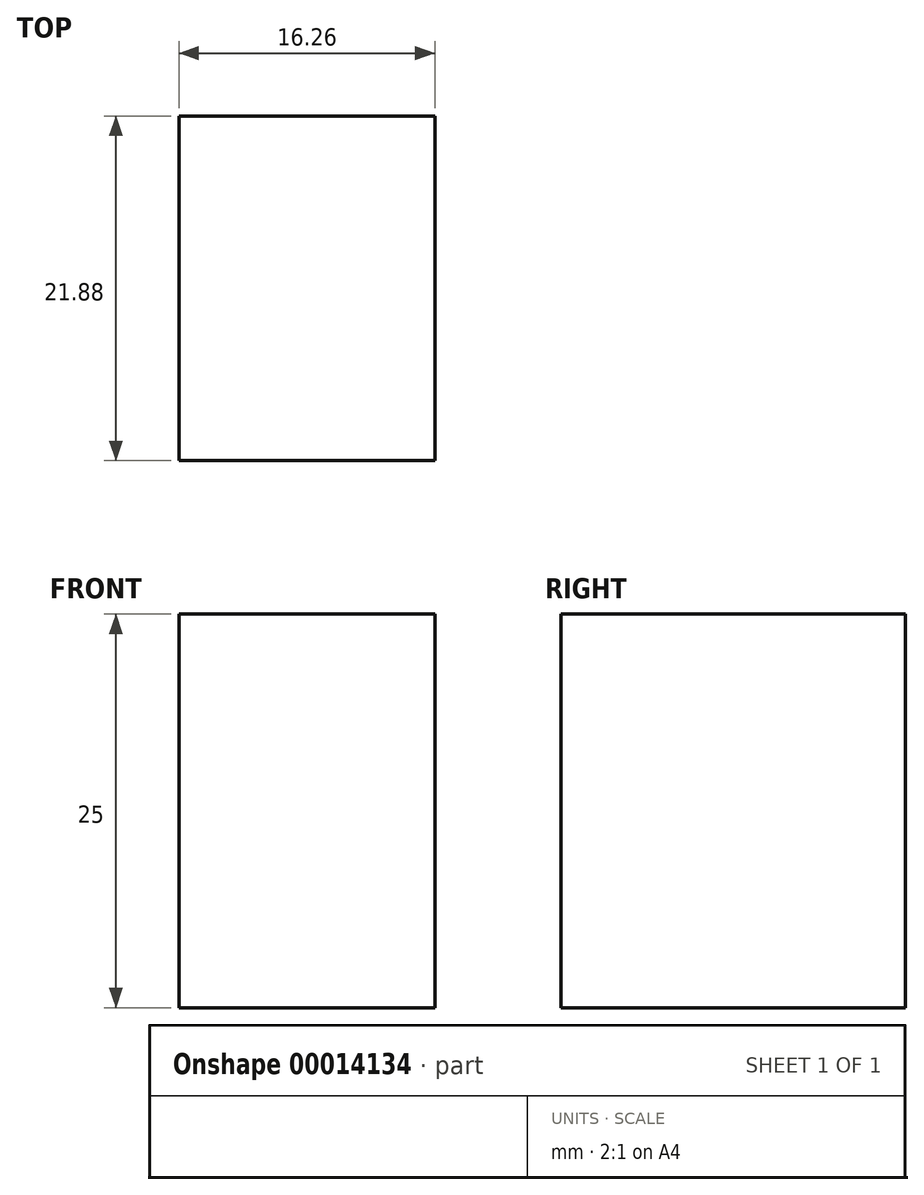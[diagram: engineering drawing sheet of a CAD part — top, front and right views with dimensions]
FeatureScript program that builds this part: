
annotation { "Feature Type Name" : "Feature", "Feature Type Description" : "" }
export const myFeature = defineFeature(function(context is Context, id is Id, definition is map)
    precondition{}
    {
        {
            var Q0;
            Q0=qCreatedBy(makeId("Front.planeOp"),FACE);
            var sketch = newSketch(context, id + "F0", { "sketchPlane" : qUnion([Q0])});
            skLineSegment(sketch, "E0", {"start": v(0, 0) * mm, "end": v(0, 450) * mm});
            skLineSegment(sketch, "E1", {"start": v(0, 0) * mm, "end": v(450, 0) * mm});
            skSolve(sketch);
        }
        {
            var Q0;
            Q0=qCreatedBy(makeId("Top.planeOp"),FACE);
            var sketch = newSketch(context, id + "F1", { "sketchPlane" : qUnion([Q0])});
            skLineSegment(sketch, "E2.rect.bottom", {"start": v(8.13, 10.94) * mm, "end": v(-8.13, 10.94) * mm});
            skLineSegment(sketch, "E2.rect.top", {"start": v(8.13, -10.94) * mm, "end": v(-8.13, -10.94) * mm});
            skLineSegment(sketch, "E2.rect.left", {"start": v(8.13, 10.94) * mm, "end": v(8.13, -10.94) * mm});
            skLineSegment(sketch, "E2.rect.right", {"start": v(-8.13, 10.94) * mm, "end": v(-8.13, -10.94) * mm});
            skPoint(sketch, "E2.rect.middle", {"position": v(0, 0) * mm});
            skSolve(sketch);
        }
        {
            var Q0;
            Q0=qSketchRegion(id+"F1",true);
            extrude(context, id + "F2", {"entities" : qUnion([Q0]), "endBound" : BoundingType.SYMMETRIC, "depth" : 25 * mm});
        }
    });
